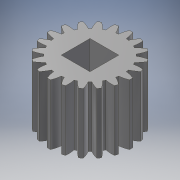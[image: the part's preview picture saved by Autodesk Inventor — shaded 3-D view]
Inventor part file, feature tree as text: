
AUTODESK INVENTOR PART (.ipt)
format: ipt  version: 2017 (Build 210142000, 142)  size: 226,816 bytes
history: native  units: mm (DEFAULTED — no unit token found)
features: sketch x4, plane x3, other x3, extrude x2
ambient origin geometry x8: Origin, YZ Plane, XZ Plane, XY Plane, X Axis, Y Axis, Z Axis, Center Point
bodies: Solid1 (feature_tree)
feature tree (12):
  extrude  "Extrusion1"  Depth=20.0mm TaperAngle=0.0deg
  plane  "Work Plane2"
  plane  "Work Plane8"
  plane  "Work Plane9"
  other  "Spur Gear"
  extrude  "Extrusion2"  Depth=10.0mm TaperAngle=0.0deg
  sketch  "Sketch4"  dims[d17=0.0mm d34=1.570796mm d39=0.0mm d41=0.0mm d43=24.87348mm d46=24.87348mm d47=0.0mm d48=0.0mm d49=9.525mm d50=10.0mm d51=0.0mm]
  sketch  "Sketch1"  dims[d0=27.24696mm d1=20.0mm d2=0.0mm]
  sketch  "Sketch2"  dims[d3=24.87348mm d4=10.0mm d5=0.0mm]
  other  "Srf1"
  sketch  "Sketch3"  dims[d16=24.87348mm]
  other  "Pitch Diameter"
